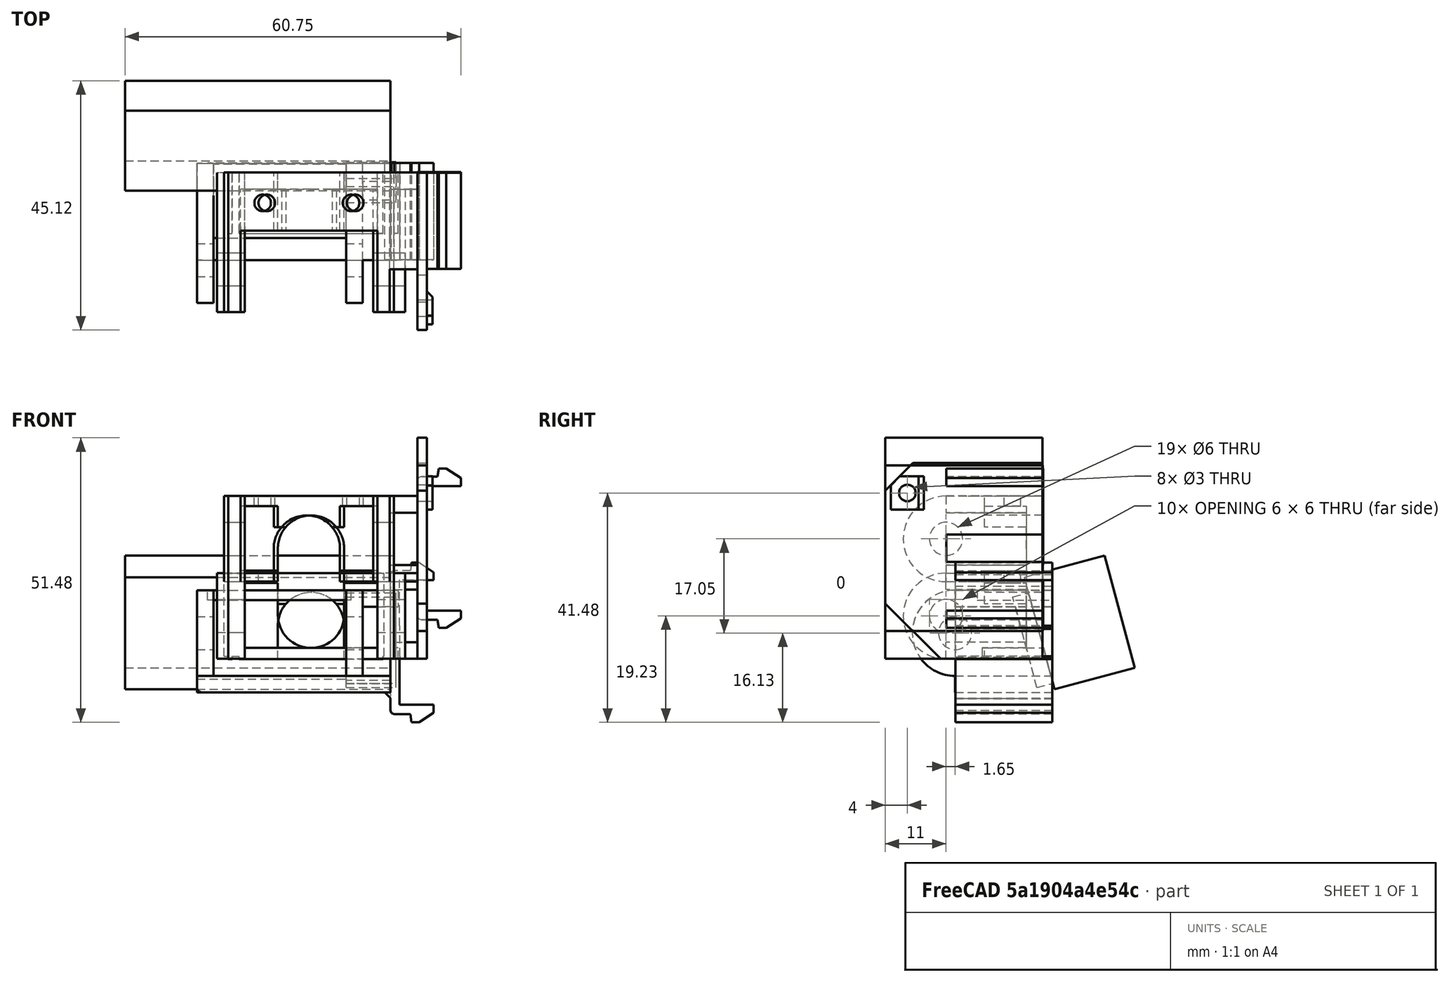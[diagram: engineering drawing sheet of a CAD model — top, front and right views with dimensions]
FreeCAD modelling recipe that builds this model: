
FCSTD DOCUMENT  (FreeCAD 0.18R14555 (Git shallow))
Label: bed-dragchain-bottom
License: All rights reserved
LicenseURL: http://en.wikipedia.org/wiki/All_rights_reserved
objects: Part::Box×32, Part::MultiFuse×15, Part::Feature×15, Part::Cut×12, Part::Cylinder×8, Part::Chamfer×8, Part::MultiCommon×4
note: 94 computed .brp shape members not serialized (recipe doc carries the construction recipe); baked Part::Feature solids carry a one-line shape summary decoded from their .brp

FEATURE [Part::Cylinder] Cylinder
  Angle = 360
  AttacherType = Attacher::AttachEngine3D
  Height = 3
  Radius = 7.75
  expr: Radius = 15.5 / 2
FEATURE [Part::Cylinder] Cylinder001
  Angle = 360
  AttacherType = Attacher::AttachEngine3D
  Height = 3
  Radius = 3
FEATURE [Part::Box] Box  label="Cube"
  AttacherType = Attacher::AttachEngine3D
  Height = 3
  Length = 15.5
  Placement = pos=(-7.75,0,0) rot=(0,0,1;0rad)
  Width = 17.5
FEATURE [Part::MultiFuse] Fusion
  Shapes = -> [Cylinder,Box]
FEATURE [Part::Cut] Cut  label="left"
  Base = -> Fusion
  Placement = pos=(-6,0,1e-15) rot=(0,1,0;1.5708rad)
  Tool = -> Cylinder001
FEATURE [Part::Feature] Cut001  label="right"
  Placement = pos=(21,0,-9e-15) rot=(0,1,0;1.5708rad)
  shape: bbox 3 x 25.25 x 15.5 mm, 11 faces (baked)
FEATURE [Part::Box] Box001  label="Cube001"
  AttacherType = Attacher::AttachEngine3D
  Height = 3
  Length = 35
  Placement = pos=(-6,0,-10.75) rot=(0,0,1;0rad)
  Width = 17.5
FEATURE [Part::Feature] Fusion001_solid  label="Fusion001 (Solid)"
  Placement = pos=(1.9,-66.314,134) rot=(0,0,-1;1.5708rad)
  shape: bbox 7.85 x 22 x 28.86 mm, 47 faces (baked)
FEATURE [Part::Box] Box002  label="Cube002"
  AttacherType = Attacher::AttachEngine3D
  Height = 3
  Length = 9
  Placement = pos=(22.5,1.65,-4.55) rot=(0,0,1;0rad)
  Width = 17.5
FEATURE [Part::Box] Box004  label="Cube004"
  AttacherType = Attacher::AttachEngine3D
  Height = 35
  Length = 49
  Placement = pos=(-4.6,19.2056,-27.1911) rot=(0,0,1;0rad)
  Width = 13
FEATURE [Part::Box] Box005  label="Cube005"
  AttacherType = Attacher::AttachEngine3D
  Height = 17
  Length = 9
  Placement = pos=(22.1,16.4525,-19.1777) rot=(1,0,0;0.261799rad)
  Width = 3
FEATURE [Part::Box] Box006  label="Cube006"
  AttacherType = Attacher::AttachEngine3D
  Height = 21
  Length = 48
  Placement = pos=(-17.9,19.635,-19.4637) rot=(1,0,0;0.261799rad)
  Width = 15
FEATURE [Part::MultiFuse] Fusion001
  Placement = pos=(1.1,1.65,-9.3) rot=(0,0,1;0rad)
  Shapes = -> [Box001,Cut,Cut001]
FEATURE [Part::MultiFuse] Fusion002
  Shapes = -> [Fusion001_solid,Fusion001]
FEATURE [Part::Chamfer] Chamfer
  Base = -> Fusion002
  Edges = 1 edges r=1: [Edge88]
FEATURE [Part::Feature] Fillet001001  label="Fillet002"
  shape: bbox 42.85 x 25.31 x 28.86 mm, 75 faces (baked)
FEATURE [Part::Feature] Fillet001001_solid  label="Fillet002 (Solid)"
  shape: bbox 42.85 x 25.31 x 28.86 mm, 75 faces (baked)
FEATURE [Part::MultiFuse] Fusion003
  Shapes = -> [Box002,Chamfer]
FEATURE [Part::Box] Box007  label="Cube007"
  AttacherType = Attacher::AttachEngine3D
  Height = 1.8
  Length = 26
  Placement = pos=(-3,5.65,-3.35) rot=(0,0,1;0rad)
  Width = 16
FEATURE [Part::MultiFuse] Fusion004
  Shapes = -> [Box007,Fusion003]
FEATURE [Part::Cut] Cut002
  Base = -> Fusion004
  Placement = pos=(-0.1,-1.65,20.05) rot=(0,0,1;0rad)
  Tool = -> Box004
FEATURE [Part::Feature] Cut002001  label="Cut003"
  shape: bbox 42.85 x 25.31 x 28.86 mm, 70 faces (baked)
FEATURE [Part::Feature] Cut002001_solid  label="Cut003 (Solid)"
  shape: bbox 42.85 x 25.31 x 28.86 mm, 70 faces (baked)
FEATURE [Part::Box] Box008  label="Cube008"
  AttacherType = Attacher::AttachEngine3D
  Height = 5
  Length = 35
  Placement = pos=(-5,0,-2) rot=(0,0,1;0rad)
  Width = 17.5
FEATURE [Part::Cut] Cut002002
  Base = -> Cut002
  Placement = pos=(5,0,-3) rot=(0,0,1;0rad)
  Tool = -> Box008
FEATURE [Part::Box] Box009  label="Cube009"
  AttacherType = Attacher::AttachEngine3D
  Height = 15
  Length = 36
  Placement = pos=(0,14.5,0) rot=(0,0,1;0rad)
  Width = 3
FEATURE [Part::Box] Box010  label="cut wall"
  AttacherType = Attacher::AttachEngine3D
  Height = 41
  Length = 56
  Placement = pos=(0,17.5,-10) rot=(0,0,1;0rad)
  Width = 3
FEATURE [Part::Cylinder] Cylinder002
  Angle = 360
  AttacherType = Attacher::AttachEngine3D
  Height = 22
  Placement = pos=(15,18,6) rot=(1,0,0;1.5708rad)
  Radius = 6
FEATURE [Part::Box] Box011  label="Cube010"
  AttacherType = Attacher::AttachEngine3D
  Height = 6
  Length = 12
  Placement = pos=(9,-4,0) rot=(0,0,1;0rad)
  Width = 22
FEATURE [Part::Box] Box012  label="Cube011"
  AttacherType = Attacher::AttachEngine3D
  Height = 3
  Length = 8
  Placement = pos=(28,0,0) rot=(0,0,1;0rad)
  Width = 16
FEATURE [Part::Box] Box013  label="Cube012"
  AttacherType = Attacher::AttachEngine3D
  Height = 30
  Length = 1.75
  Placement = pos=(35,-11,-8.95) rot=(0,0,1;0rad)
  Width = 28.5
FEATURE [Part::Cylinder] Cylinder003
  Angle = 360
  AttacherType = Attacher::AttachEngine3D
  Height = 10
  Placement = pos=(31,-7,16.05) rot=(0,1,0;1.5708rad)
  Radius = 1.5
FEATURE [Part::Box] Box015  label="Cube014"
  AttacherType = Attacher::AttachEngine3D
  Height = 2
  Length = 9
  Placement = pos=(0,4,0) rot=(0,0,1;0rad)
  Width = 13.5
FEATURE [Part::Box] Box016  label="Cube015"
  AttacherType = Attacher::AttachEngine3D
  Height = 2
  Length = 6
  Placement = pos=(21,4,0) rot=(0,0,1;0rad)
  Width = 13.5
FEATURE [Part::Cylinder] Cylinder004
  Angle = 360
  AttacherType = Attacher::AttachEngine3D
  Height = 10
  Placement = pos=(7,12,10) rot=(0,0,1;0rad)
  Radius = 1.5
FEATURE [Part::Cylinder] Cylinder005
  Angle = 360
  AttacherType = Attacher::AttachEngine3D
  Height = 10
  Placement = pos=(23,12,10) rot=(0,0,1;0rad)
  Radius = 1.5
FEATURE [Part::Box] Box017  label="Cube016"
  AttacherType = Attacher::AttachEngine3D
  Height = 4
  Length = 12
  Placement = pos=(9,4,9.9) rot=(0,0,1;0rad)
  Width = 13
FEATURE [Part::MultiFuse] Fusion006
  Shapes = -> [Box016,Box015,Box013,Box012,Box009,Cut002002,Box017]
FEATURE [Part::MultiFuse] Fusion007
  Shapes = -> [Cylinder002,Cylinder003,Cylinder005,Cylinder004,Box011]
FEATURE [Part::Box] Box018  label="Cube017"
  AttacherType = Attacher::AttachEngine3D
  Height = 25
  Length = 24
  Placement = pos=(3,0,0) rot=(0,0,1;0rad)
  Width = 7
FEATURE [Part::MultiFuse] Fusion008
  Shapes = -> [Fusion007,Box018]
FEATURE [Part::Cut] Cut002003
  Base = -> Fusion006
  Tool = -> Fusion008
FEATURE [Part::Cut] Cut002004
  Base = -> Cut002003
  Tool = -> Box010
FEATURE [Part::Feature] Cut002004001  label="Cut002005"
  shape: bbox 42.85 x 28.56 x 30 mm, 167 faces (baked)
FEATURE [Part::Feature] Cut002004002  label="Cut002006"
  shape: bbox 42.85 x 28.56 x 30 mm, 167 faces (baked)
FEATURE [Part::Box] Box019  label="Cube018"
  AttacherType = Attacher::AttachEngine3D
  Height = 19
  Length = 35
  Placement = pos=(-1,-19,0) rot=(0,0,1;0rad)
  Width = 42
FEATURE [Part::Box] Box020  label="Cube019"
  AttacherType = Attacher::AttachEngine3D
  Height = 19
  Length = 35
  Placement = pos=(-1,-19,0) rot=(0,0,1;0rad)
  Width = 42
FEATURE [Part::MultiCommon] Common
  Placement = pos=(0.75,0,0) rot=(0,0,1;0rad)
  Shapes = -> [Cut002004002,Box019]
FEATURE [Part::Cut] Cut002004003
  Base = -> Cut002004001
  Tool = -> Box020
FEATURE [Part::MultiFuse] Fusion009
  Shapes = -> [Common,Cut002004003]
FEATURE [Part::Feature] Fusion009001  label="Fusion010"
  shape: bbox 42.1 x 28.56 x 30 mm, 88 faces (baked)
FEATURE [Part::Box] Box021  label="Cube020"
  AttacherType = Attacher::AttachEngine3D
  Height = 23
  Length = 35
  Placement = pos=(0,-11,-4) rot=(0,0,1;0rad)
  Width = 37
FEATURE [Part::Feature] Fusion009002  label="Fusion011"
  shape: bbox 42.1 x 28.56 x 30 mm, 88 faces (baked)
FEATURE [Part::Box] Box022  label="Cube021"
  AttacherType = Attacher::AttachEngine3D
  Height = 23
  Length = 35
  Placement = pos=(0,-11,-4) rot=(0,0,1;0rad)
  Width = 37
FEATURE [Part::MultiCommon] Common001
  Placement = pos=(0,0,-13.95) rot=(0,0,1;0rad)
  Shapes = -> [Fusion009002,Box022]
FEATURE [Part::Cut] Cut002004004
  Base = -> Fusion009001
  Tool = -> Box021
FEATURE [Part::Box] Box023  label="Cube022"
  AttacherType = Attacher::AttachEngine3D
  Height = 18
  Length = 1.75
  Placement = pos=(35,-11,-13.95) rot=(0,0,1;0rad)
  Width = 28.5
FEATURE [Part::Box] Box024  label="wall-2"
  AttacherType = Attacher::AttachEngine3D
  Height = 51
  Length = 48
  Placement = pos=(-4.5,17.4439,-16.45) rot=(0,0,1;0rad)
  Width = 28.5
FEATURE [Part::Box] Box025  label="Cube023"
  AttacherType = Attacher::AttachEngine3D
  Height = 6
  Length = 1.75
  Placement = pos=(35,-11,20.05) rot=(0,0,1;0rad)
  Width = 28.5
FEATURE [Part::MultiFuse] Fusion009003
  Shapes = -> [Box025,Box023,Cut002004004,Common001]
FEATURE [Part::Cut] Cut002004005
  Base = -> Fusion009003
  Tool = -> Box024
FEATURE [Part::Feature] Cut002004005001  label="Cut002004006"
  shape: bbox 42.1 x 28.44 x 40 mm, 59 faces (baked)
FEATURE [Part::Chamfer] Chamfer001
  Base = -> Cut002004005001
  Edges = 3 edges r=0.5: [Edge55,Edge138,Edge143]
FEATURE [Part::Chamfer] Chamfer002
  Base = -> Chamfer001
  Edges = 2 edges r=4: [Edge26,Edge63]
FEATURE [Part::Chamfer] Chamfer003
  Base = -> Chamfer002
  Edges = 1 edges r=10: [Edge94]
FEATURE [Part::Chamfer] Chamfer004
  Base = -> Chamfer003
  Edges = 2 edges r=0.5: [Edge69,Edge70]
FEATURE [Part::Box] Box026  label="Cube024"
  AttacherType = Attacher::AttachEngine3D
  Height = 10
  Length = 11
  Placement = pos=(27.5,-15.5,21.5) rot=(0,0,1;0rad)
  Width = 37
FEATURE [Part::Cut] Cut002004005002
  Base = -> Chamfer004
  Tool = -> Box026
FEATURE [Part::Chamfer] Chamfer005
  Base = -> Cut002004005002
  Edges = 1 edges r=5: [Edge156]
FEATURE [Part::Box] Box027  label="Cube025"
  AttacherType = Attacher::AttachEngine3D
  Height = 19
  Length = 24
  Placement = pos=(3.75,5,-17) rot=(0,0,1;0rad)
  Width = 20
FEATURE [Part::Cut] Cut002004005003
  Base = -> Chamfer005
  Tool = -> Box027
FEATURE [Part::Box] Box028  label="Cube026"
  AttacherType = Attacher::AttachEngine3D
  Height = 2
  Length = 26
  Placement = pos=(2.75,6.5,-14) rot=(0,0,1;0rad)
  Width = 11
FEATURE [Part::MultiFuse] Fusion009004
  Shapes = -> [Box028,Cut002004005003]
FEATURE [Part::Box] Box029  label="Cube027"
  AttacherType = Attacher::AttachEngine3D
  Height = 18
  Length = 3.5
  Placement = pos=(0,-10,-14) rot=(0,0,1;0rad)
  Width = 31
FEATURE [Part::Feature] Fusion009004001  label="Fusion009005"
  shape: bbox 42.1 x 28.5 x 35.5 mm, 55 faces (baked)
FEATURE [Part::Feature] Fusion009004002  label="Fusion009006"
  shape: bbox 42.1 x 28.5 x 35.5 mm, 55 faces (baked)
FEATURE [Part::Box] Box030  label="Cube028"
  AttacherType = Attacher::AttachEngine3D
  Height = 18
  Length = 2
  Placement = pos=(28,-10,-14) rot=(0,0,1;0rad)
  Width = 31
FEATURE [Part::MultiCommon] Common002
  Placement = pos=(2.75,0,0) rot=(0,0,1;0rad)
  Shapes = -> [Fusion009004002,Box030]
FEATURE [Part::MultiCommon] Common003
  Placement = pos=(-2,0,0) rot=(0,0,1;0rad)
  Shapes = -> [Fusion009004001,Box029]
FEATURE [Part::MultiFuse] Fusion009004003
  Shapes = -> [Common003,Common002,Fusion009004]
FEATURE [Part::Box] Box031  label="Cube029"
  AttacherType = Attacher::AttachEngine3D
  Height = 15
  Length = 29
  Placement = pos=(0,14.5,-13.5) rot=(0,0,1;0rad)
  Width = 3
FEATURE [Part::Cylinder] Cylinder006
  Angle = 360
  AttacherType = Attacher::AttachEngine3D
  Height = 10
  Placement = pos=(0,0,0) rot=(-1,0,0;1.5708rad)
  Radius = 6
FEATURE [Part::Box] Box032  label="Cube030"
  AttacherType = Attacher::AttachEngine3D
  Height = 10
  Length = 12
  Placement = pos=(-6,0,0) rot=(0,0,1;0rad)
  Width = 10
FEATURE [Part::MultiFuse] Fusion009004004
  Placement = pos=(15.75,14,-6) rot=(0,0,1;0rad)
  Shapes = -> [Box032,Cylinder006]
FEATURE [Part::Cut] Cut002004005004
  Base = -> Box031
  Tool = -> Fusion009004004
FEATURE [Part::MultiFuse] Fusion009004005
  Shapes = -> [Cut002004005004,Fusion009004003]
FEATURE [Part::Feature] Fusion009004005001  label="Fusion009004006"
  shape: bbox 44.1 x 28.5 x 35.5 mm, 74 faces (baked)
FEATURE [Part::Feature] Fusion009004005001_solid  label="Fusion009004006 (Solid)"
  shape: bbox 44.1 x 28.5 x 35.5 mm, 74 faces (baked)
FEATURE [Part::Cylinder] Cylinder007
  Angle = 360
  AttacherType = Attacher::AttachEngine3D
  Height = 10
  Placement = pos=(34,-7,16.05) rot=(0,1,0;1.5708rad)
  Radius = 1.5
FEATURE [Part::Box] Box033  label="Cube031"
  AttacherType = Attacher::AttachEngine3D
  Height = 6
  Length = 2
  Placement = pos=(35.75,-10,13.05) rot=(0,0,1;0rad)
  Width = 6
FEATURE [Part::Chamfer] Chamfer006
  Base = -> Box033
  Edges = 1 edges r=1: [Edge7]
FEATURE [Part::Chamfer] Chamfer007
  Base = -> Chamfer006
  Edges = 1 edges r=1.6: [Edge8]
FEATURE [Part::Cut] Cut002004005005
  Base = -> Chamfer007
  Tool = -> Cylinder007
FEATURE [Part::MultiFuse] Fusion009004005002
  Shapes = -> [Cut002004005005,Fusion009004005001_solid]
